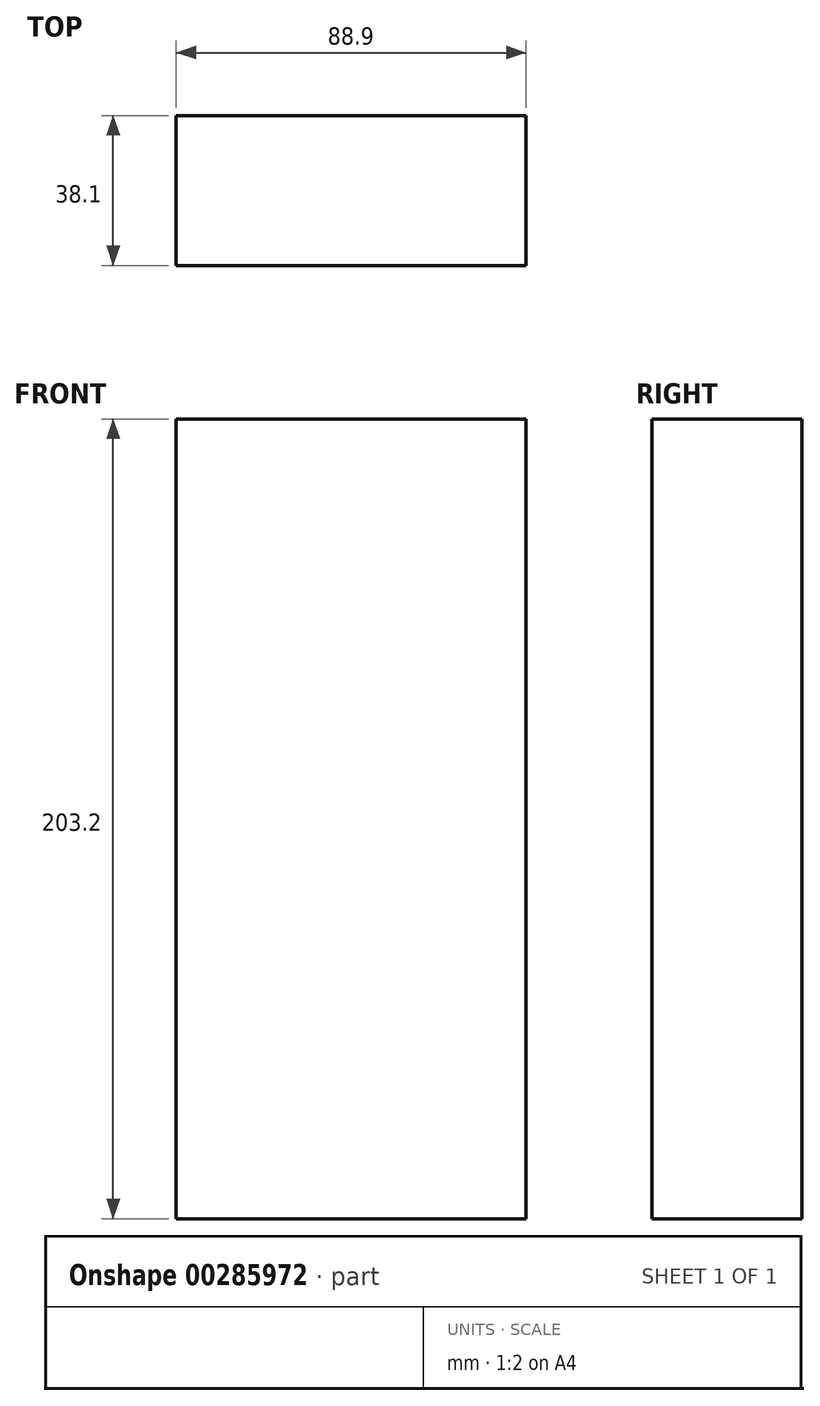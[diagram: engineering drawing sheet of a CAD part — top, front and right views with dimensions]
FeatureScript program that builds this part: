
annotation { "Feature Type Name" : "Feature", "Feature Type Description" : "" }
export const myFeature = defineFeature(function(context is Context, id is Id, definition is map)
    precondition{}
    {
        {
            var Q0;
            Q0=qCreatedBy(makeId("Top.planeOp"),FACE);
            var sketch = newSketch(context, id + "F0", { "sketchPlane" : qUnion([Q0])});
            skLineSegment(sketch, "E0.bottom", {"start": v(44.45, -19.05) * mm, "end": v(-44.45, -19.05) * mm});
            skLineSegment(sketch, "E0.top", {"start": v(44.45, 19.05) * mm, "end": v(-44.45, 19.05) * mm});
            skLineSegment(sketch, "E0.left", {"start": v(44.45, -19.05) * mm, "end": v(44.45, 19.05) * mm});
            skLineSegment(sketch, "E0.right", {"start": v(-44.45, -19.05) * mm, "end": v(-44.45, 19.05) * mm});
            skPoint(sketch, "E0.middle", {"position": v(0, 0) * mm});
            skSolve(sketch);
        }
        {
            var Q0;
            Q0=makeQuery(id+"F0.imprint","IMPRINT",FACE,{"disambiguationData":[TD([[makeQuery(id+"F0.imprint","IMPRINT",EDGE,{"derivedFrom":sQuery(id+"F0.wireOp",EDGE,"E0.bottom")}),-1.0]])]});
            extrude(context, id + "F1", {"entities" : qUnion([Q0]), "depth" : 203.2 * mm});
        }
    });
